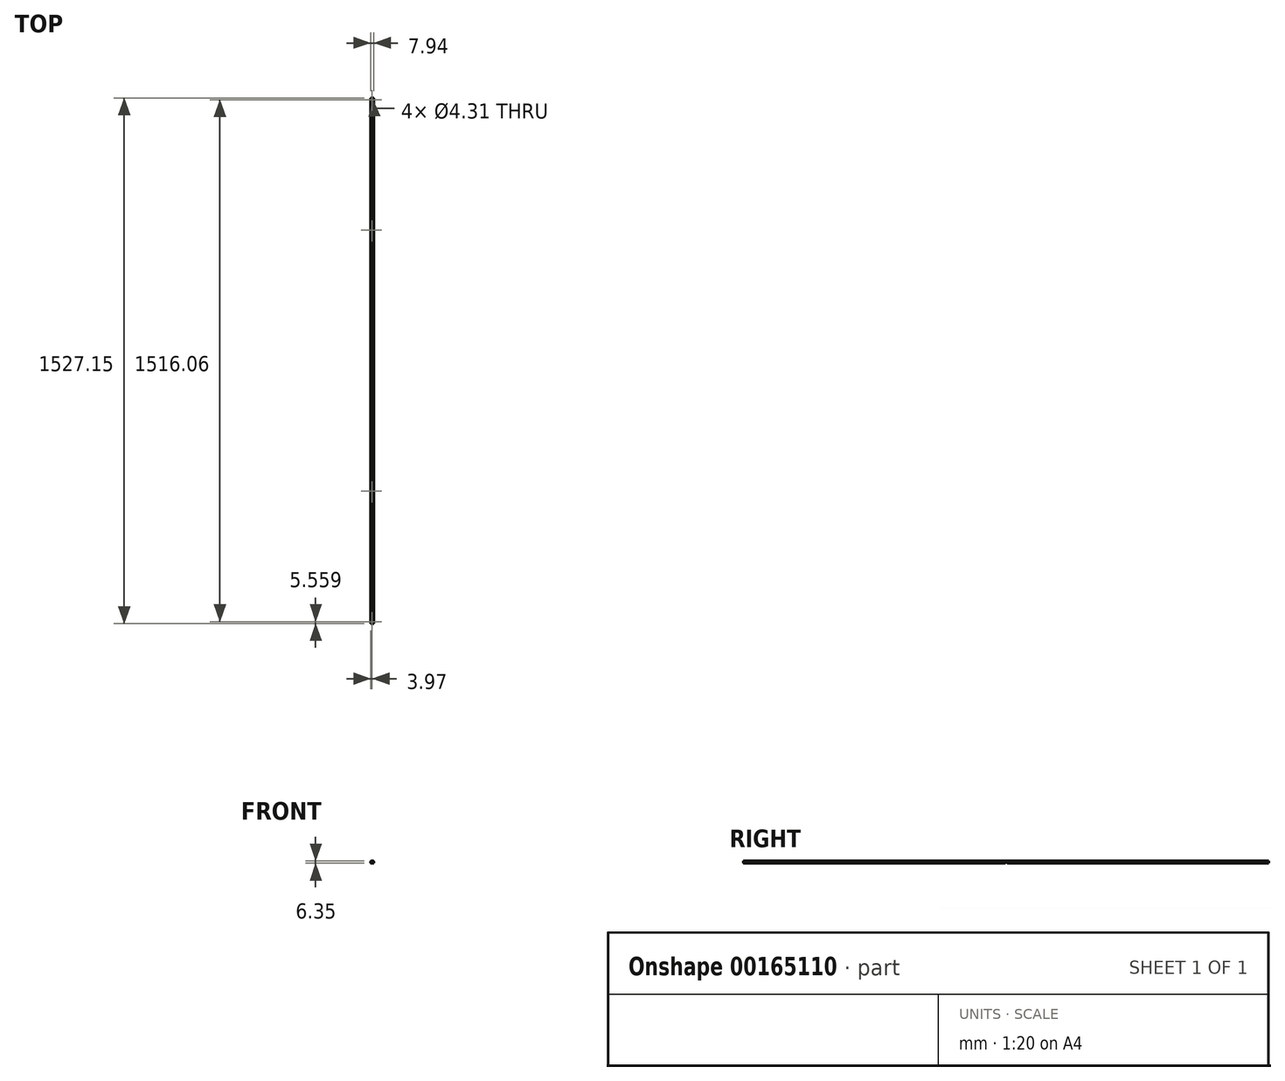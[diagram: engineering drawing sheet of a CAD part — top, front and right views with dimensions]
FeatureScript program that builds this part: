
annotation { "Feature Type Name" : "Feature", "Feature Type Description" : "" }
export const myFeature = defineFeature(function(context is Context, id is Id, definition is map)
    precondition{}
    {
        {
            var Q0;
            Q0=qCreatedBy(makeId("Top.planeOp"),FACE);
            var sketch = newSketch(context, id + "F0", { "sketchPlane" : qUnion([Q0])});
            skLineSegment(sketch, "E0.bottom", {"start": v(-3.97, 763.59) * mm, "end": v(3.97, 763.59) * mm});
            skLineSegment(sketch, "E0.top", {"start": v(-3.97, -763.59) * mm, "end": v(3.97, -763.59) * mm});
            skLineSegment(sketch, "E0.left", {"start": v(-3.97, 763.59) * mm, "end": v(-3.97, -763.59) * mm});
            skLineSegment(sketch, "E0.right", {"start": v(3.97, 763.59) * mm, "end": v(3.97, -763.59) * mm});
            skPoint(sketch, "E0.middle", {"position": v(0, 0) * mm});
            skLineSegment(sketch, "E1", {"start": v(0, -763.59) * mm, "end": v(0, -758.03) * mm, "construction": true});
            skLineSegment(sketch, "E2", {"start": v(0, 758.03) * mm, "end": v(0, 763.59) * mm, "construction": true});
            skCircle(sketch, "E3", {"center": v(0, -758.03) * mm, "radius": 2.15 * mm});
            skCircle(sketch, "E4", {"center": v(0, 758.03) * mm, "radius": 2.15 * mm});
            skLineSegment(sketch, "E5", {"start": v(0, 758.03) * mm, "end": v(0, 379.02) * mm, "construction": true});
            skLineSegment(sketch, "E6", {"start": v(0, -379.02) * mm, "end": v(0, -758.03) * mm, "construction": true});
            skCircle(sketch, "E7", {"center": v(0, 379.02) * mm, "radius": 2.15 * mm});
            skCircle(sketch, "E8", {"center": v(0, -379.02) * mm, "radius": 2.15 * mm});
            skLineSegment(sketch, "E9", {"start": v(0, 379.02) * mm, "end": v(0, 0) * mm, "construction": true});
            skLineSegment(sketch, "E10", {"start": v(0, 0) * mm, "end": v(0, -379.02) * mm, "construction": true});
            skSolve(sketch);
        }
        {
            var Q0;
            Q0=qSketchRegion(id+"F0",true);
            extrude(context, id + "F1", {"entities" : qUnion([Q0]), "depth" : 6.35 * mm});
        }
        {
            var Q0;
            Q0=makeQuery(id+"F1.opExtrude","SWEPT_FACE",FACE,{"disambiguationData":[OSD([sQuery(id+"F0.wireOp",EDGE,"E0.right")])]});
            var sketch = newSketch(context, id + "F2", { "sketchPlane" : qUnion([Q0])});
            skLineSegment(sketch, "E11.bottom", {"start": v(-3.97, 0) * mm, "end": v(3.97, 0) * mm});
            skLineSegment(sketch, "E11.top", {"start": v(-3.97, 3.17) * mm, "end": v(3.97, 3.17) * mm});
            skLineSegment(sketch, "E11.left", {"start": v(-3.97, 0) * mm, "end": v(-3.97, 3.17) * mm});
            skLineSegment(sketch, "E11.right", {"start": v(3.97, 0) * mm, "end": v(3.97, 3.17) * mm});
            skSolve(sketch);
        }
        {
            var Q0;
            Q0=qSketchRegion(id+"F2",true);
            var Q1;
            Q1=makeQuery(id+"F1.opExtrude","SWEPT_FACE",FACE,{"disambiguationData":[OSD([sQuery(id+"F0.wireOp",EDGE,"E0.left")])]});
            extrude(context, id + "F3", {"entities" : qUnion([Q0]), "operationType" : NewBodyOperationType.REMOVE, "endBound" : BoundingType.UP_TO_SURFACE, "oppositeDirection" : true, "endBoundEntityFace" : qUnion([Q1]), "depth" : 25.4 * mm});
        }
        {
            var Q0;
            Q0=makeQuery(id+"F1.opExtrude","CAP_FACE",FACE,{"disambiguationData":[OSD([sQuery(id+"F0.wireOp",EDGE,"E0.bottom"),sQuery(id+"F0.wireOp",EDGE,"E0.top"),sQuery(id+"F0.wireOp",EDGE,"E0.left"),sQuery(id+"F0.wireOp",EDGE,"E0.right"),sQuery(id+"F0.wireOp",EDGE,"E3"),sQuery(id+"F0.wireOp",EDGE,"E4")])],"isStart":false});
            var sketch = newSketch(context, id + "F4", { "sketchPlane" : qUnion([Q0])});
            skLineSegment(sketch, "E12", {"start": v(0, 763.59) * mm, "end": v(3.97, 762.52) * mm});
            skLineSegment(sketch, "E13", {"start": v(0, 763.59) * mm, "end": v(-3.97, 762.52) * mm});
            skLineSegment(sketch, "E14.bottom", {"start": v(-3.97, 762.52) * mm, "end": v(3.97, 762.52) * mm, "construction": true});
            skLineSegment(sketch, "E14.top", {"start": v(-3.97, 770.46) * mm, "end": v(3.97, 770.46) * mm});
            skLineSegment(sketch, "E14.left", {"start": v(-3.97, 762.52) * mm, "end": v(-3.97, 770.46) * mm});
            skLineSegment(sketch, "E14.right", {"start": v(3.97, 762.52) * mm, "end": v(3.97, 770.46) * mm});
            skSolve(sketch);
        }
        {
            var Q0;
            Q0 = qSketchRegion(id + "F4", true);
            var Q1;
            {var subQ0=sQuery(id+"F0.wireOp",EDGE,"E4");var subQ1=sQuery(id+"F0.wireOp",EDGE,"E0.left");var subQ2=sQuery(id+"F0.wireOp",EDGE,"E0.right");var subQ3=sQuery(id+"F0.wireOp",EDGE,"E0.bottom");var subQ4=sQuery(id+"F0.wireOp",EDGE,"E7");Q1=makeQuery(id+"F3.boolean.opBoolean","SPLIT",FACE,{"disambiguationData":[TD([makeQuery(id+"F1.opExtrude","SWEPT_FACE",FACE,{"disambiguationData":[OSD([subQ3])]})])],"derivedFrom":makeQuery(id+"F1.opExtrude","CAP_FACE",FACE,{"disambiguationData":[OSD([subQ3,sQuery(id+"F0.wireOp",EDGE,"E0.top"),subQ1,subQ2,sQuery(id+"F0.wireOp",EDGE,"E3"),subQ0,subQ4,sQuery(id+"F0.wireOp",EDGE,"E8")])],"isStart":true})});}
            extrude(context, id + "F5", {"entities" : qUnion([Q0]), "operationType" : NewBodyOperationType.REMOVE, "endBound" : BoundingType.UP_TO_SURFACE, "oppositeDirection" : true, "endBoundEntityFace" : qUnion([Q1]), "depth" : 25.4 * mm});
        }
        {
            var Q0;
            Q0=makeQuery(id+"F5.boolean.opBoolean","COPY",EDGE,{"derivedFrom":makeQuery(id+"F5.opExtrude","CAP_EDGE",EDGE,{"disambiguationData":[OSD([sQuery(id+"F4.wireOp",EDGE,"E13")])],"isStart":true})});
            var Q1;
            Q1=makeQuery(id+"F5.boolean.opBoolean","COPY",EDGE,{"derivedFrom":makeQuery(id+"F5.opExtrude","CAP_EDGE",EDGE,{"disambiguationData":[OSD([sQuery(id+"F4.wireOp",EDGE,"E12")])],"isStart":true})});
            var Q2;
            Q2=makeQuery(id+"F5.boolean.opBoolean","COPY",EDGE,{"derivedFrom":makeQuery(id+"F5.opExtrude","SWEPT_EDGE",EDGE,{"disambiguationData":[OSD([sQuery(id+"F0.wireOp",EDGE,"E0.bottom"),sQuery(id+"F4.wireOp",EDGE,"E12"),sQuery(id+"F4.wireOp",EDGE,"E13")])]})});
            var Q3;
            Q3=makeQuery(id+"F5.boolean.opBoolean","COPY",EDGE,{"derivedFrom":makeQuery(id+"F5.opExtrude","SWEPT_EDGE",EDGE,{"disambiguationData":[OSD([sQuery(id+"F0.wireOp",EDGE,"E0.right"),sQuery(id+"F4.wireOp",EDGE,"E12"),sQuery(id+"F4.wireOp",EDGE,"E14.right")])]})});
            var Q4;
            Q4=makeQuery(id+"F5.boolean.opBoolean","COPY",EDGE,{"derivedFrom":makeQuery(id+"F5.opExtrude","SWEPT_EDGE",EDGE,{"disambiguationData":[OSD([sQuery(id+"F0.wireOp",EDGE,"E0.left"),sQuery(id+"F4.wireOp",EDGE,"E13"),sQuery(id+"F4.wireOp",EDGE,"E14.left")])]})});
            var Q5;
            Q5=makeQuery(id+"F1.opExtrude","CAP_EDGE",EDGE,{"disambiguationData":[OSD([sQuery(id+"F0.wireOp",EDGE,"E0.left")])],"isStart":false});
            var Q6;
            Q6=makeQuery(id+"F1.opExtrude","CAP_EDGE",EDGE,{"disambiguationData":[OSD([sQuery(id+"F0.wireOp",EDGE,"E0.right")])],"isStart":false});
            var Q7;
            {var subQ0=sQuery(id+"F0.wireOp",EDGE,"E0.bottom");var subQ1=sQuery(id+"F0.wireOp",EDGE,"E0.left");Q7=makeQuery(id+"F3.boolean.opBoolean","SPLIT",EDGE,{"disambiguationData":[TD([makeQuery(id+"F1.opExtrude","SWEPT_FACE",FACE,{"disambiguationData":[OSD([subQ0])]})])],"derivedFrom":makeQuery(id+"F1.opExtrude","CAP_EDGE",EDGE,{"disambiguationData":[OSD([subQ1])],"isStart":true})});}
            var Q8;
            Q8=makeQuery(id+"F5.boolean.opBoolean","COPY",EDGE,{"derivedFrom":makeQuery(id+"F5.opExtrude","CAP_EDGE",EDGE,{"disambiguationData":[OSD([sQuery(id+"F4.wireOp",EDGE,"E13")])],"isStart":false})});
            var Q9;
            Q9=makeQuery(id+"F5.boolean.opBoolean","COPY",EDGE,{"derivedFrom":makeQuery(id+"F5.opExtrude","CAP_EDGE",EDGE,{"disambiguationData":[OSD([sQuery(id+"F4.wireOp",EDGE,"E12")])],"isStart":false})});
            var Q10;
            {var subQ0=sQuery(id+"F0.wireOp",EDGE,"E0.bottom");var subQ1=sQuery(id+"F0.wireOp",EDGE,"E0.right");Q10=makeQuery(id+"F3.boolean.opBoolean","SPLIT",EDGE,{"disambiguationData":[TD([makeQuery(id+"F1.opExtrude","SWEPT_FACE",FACE,{"disambiguationData":[OSD([subQ0])]})])],"derivedFrom":makeQuery(id+"F1.opExtrude","CAP_EDGE",EDGE,{"disambiguationData":[OSD([subQ1])],"isStart":true})});}
            var Q11;
            Q11=makeQuery(id+"F1.opExtrude","SWEPT_EDGE",EDGE,{"disambiguationData":[OSD([sQuery(id+"F0.wireOp",EDGE,"E0.top"),sQuery(id+"F0.wireOp",EDGE,"E0.right")])]});
            var Q12;
            {var subQ0=sQuery(id+"F0.wireOp",EDGE,"E0.right");var subQ1=sQuery(id+"F0.wireOp",EDGE,"E0.top");Q12=makeQuery(id+"F3.boolean.opBoolean","SPLIT",EDGE,{"disambiguationData":[TD([makeQuery(id+"F1.opExtrude","SWEPT_FACE",FACE,{"disambiguationData":[OSD([subQ1])]})])],"derivedFrom":makeQuery(id+"F1.opExtrude","CAP_EDGE",EDGE,{"disambiguationData":[OSD([subQ0])],"isStart":true})});}
            var Q13;
            Q13=makeQuery(id+"F1.opExtrude","CAP_EDGE",EDGE,{"disambiguationData":[OSD([sQuery(id+"F0.wireOp",EDGE,"E0.top")])],"isStart":true});
            var Q14;
            Q14=makeQuery(id+"F1.opExtrude","SWEPT_EDGE",EDGE,{"disambiguationData":[OSD([sQuery(id+"F0.wireOp",EDGE,"E0.top"),sQuery(id+"F0.wireOp",EDGE,"E0.left")])]});
            var Q15;
            Q15=makeQuery(id+"F1.opExtrude","CAP_EDGE",EDGE,{"disambiguationData":[OSD([sQuery(id+"F0.wireOp",EDGE,"E0.top")])],"isStart":false});
            var Q16;
            {var subQ0=sQuery(id+"F0.wireOp",EDGE,"E0.left");var subQ1=sQuery(id+"F0.wireOp",EDGE,"E0.top");Q16=makeQuery(id+"F3.boolean.opBoolean","SPLIT",EDGE,{"disambiguationData":[TD([makeQuery(id+"F1.opExtrude","SWEPT_FACE",FACE,{"disambiguationData":[OSD([subQ1])]})])],"derivedFrom":makeQuery(id+"F1.opExtrude","CAP_EDGE",EDGE,{"disambiguationData":[OSD([subQ0])],"isStart":true})});}
            fillet(context, id + "F6", {"entities" : qUnion([Q0, Q1, Q2, Q3, Q4, Q5, Q6, Q7, Q8, Q9, Q10, Q11, Q12, Q13, Q14, Q15, Q16]), "radius" : 0.76 * mm, "tangentPropagation" : true, "allowEdgeOverflow" : false});
        }
    });
